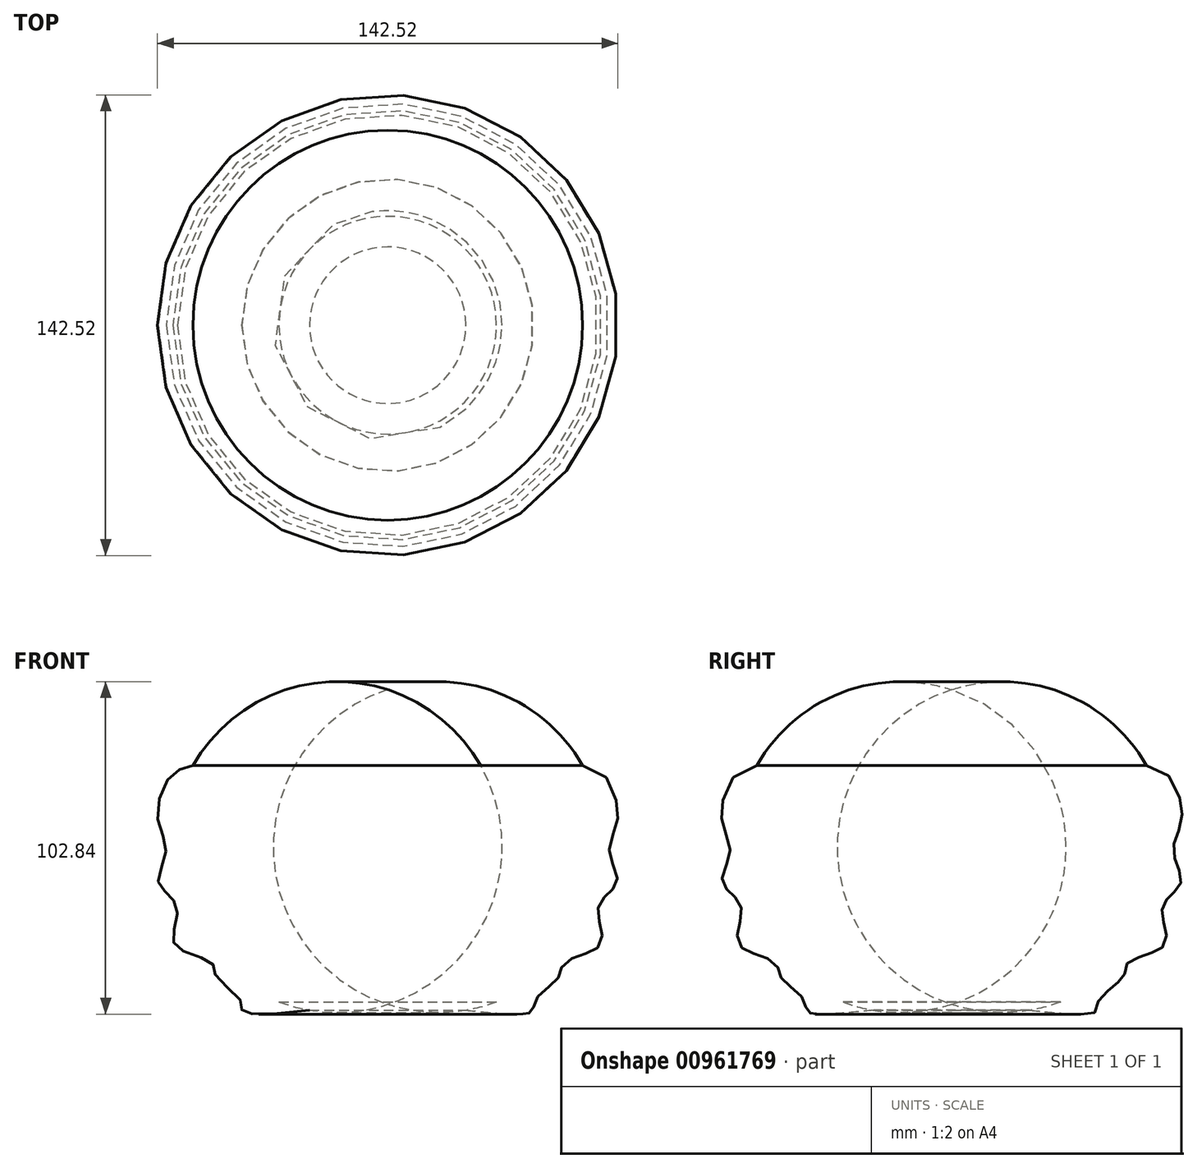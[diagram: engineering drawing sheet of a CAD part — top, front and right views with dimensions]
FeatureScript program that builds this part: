
annotation { "Feature Type Name" : "Feature", "Feature Type Description" : "" }
export const myFeature = defineFeature(function(context is Context, id is Id, definition is map)
    precondition{}
    {
        {
            var Q0;
            Q0=qCreatedBy(makeId("Front.planeOp"),FACE);
            var sketch = newSketch(context, id + "F0", { "sketchPlane" : qUnion([Q0])});
            skArc(sketch, "E0", {"start": v(-60.3, 0) * mm, "mid": v(-63.84, -42.7) * mm, "end": v(-33.66, -73.12) * mm});
            skLineSegment(sketch, "E1", {"start": v(-24.21, -75.65) * mm, "end": v(0, -75.65) * mm});
            skLineSegment(sketch, "E2", {"start": v(0, -75.65) * mm, "end": v(0, 0) * mm});
            skFitSpline(sketch, "E3", {"points": [v(-60.3, 0) * mm, v(-67.04, -3) * mm, v(-71.16, -16.56) * mm, v(-68.55, -26.27) * mm, v(-71.04, -35.21) * mm, v(-68.53, -39.32) * mm, v(-65.11, -44.3) * mm, v(-66.45, -52.9) * mm, v(-63.94, -57) * mm, v(-54.21, -61.2) * mm, v(-53.38, -64.72) * mm, v(-45.35, -72.95) * mm, v(-44.98, -75.91) * mm, v(-24.21, -75.65) * mm], "startDerivative": vector(-98.14, -18.47) * mm, "endDerivative": vector(238.34, 24.5) * mm});
            skLineSegment(sketch, "E4", {"start": v(-24.21, -73.12) * mm, "end": v(0, -73.12) * mm});
            skLineSegment(sketch, "E5", {"start": v(-24.21, -73.12) * mm, "end": v(-33.66, -73.12) * mm});
            skSolve(sketch);
        }
        {
            var Q0;
            Q0=makeQuery(id+"F0.imprint","IMPRINT",FACE,{"disambiguationData":[TD([[makeQuery(id+"F0.imprint","IMPRINT",EDGE,{"derivedFrom":sQuery(id+"F0.wireOp",EDGE,"E0")}),-1.0]])]});
            var Q1;
            Q1=sQuery(id+"F0.wireOp",EDGE,"E2");
            revolve(context, id + "F1", {"surfaceOperationType" : NewSurfaceOperationType.NEW, "entities" : qUnion([Q0]), "axis" : qUnion([Q1]), "revolveType" : RevolveType.FULL});
        }
    });
